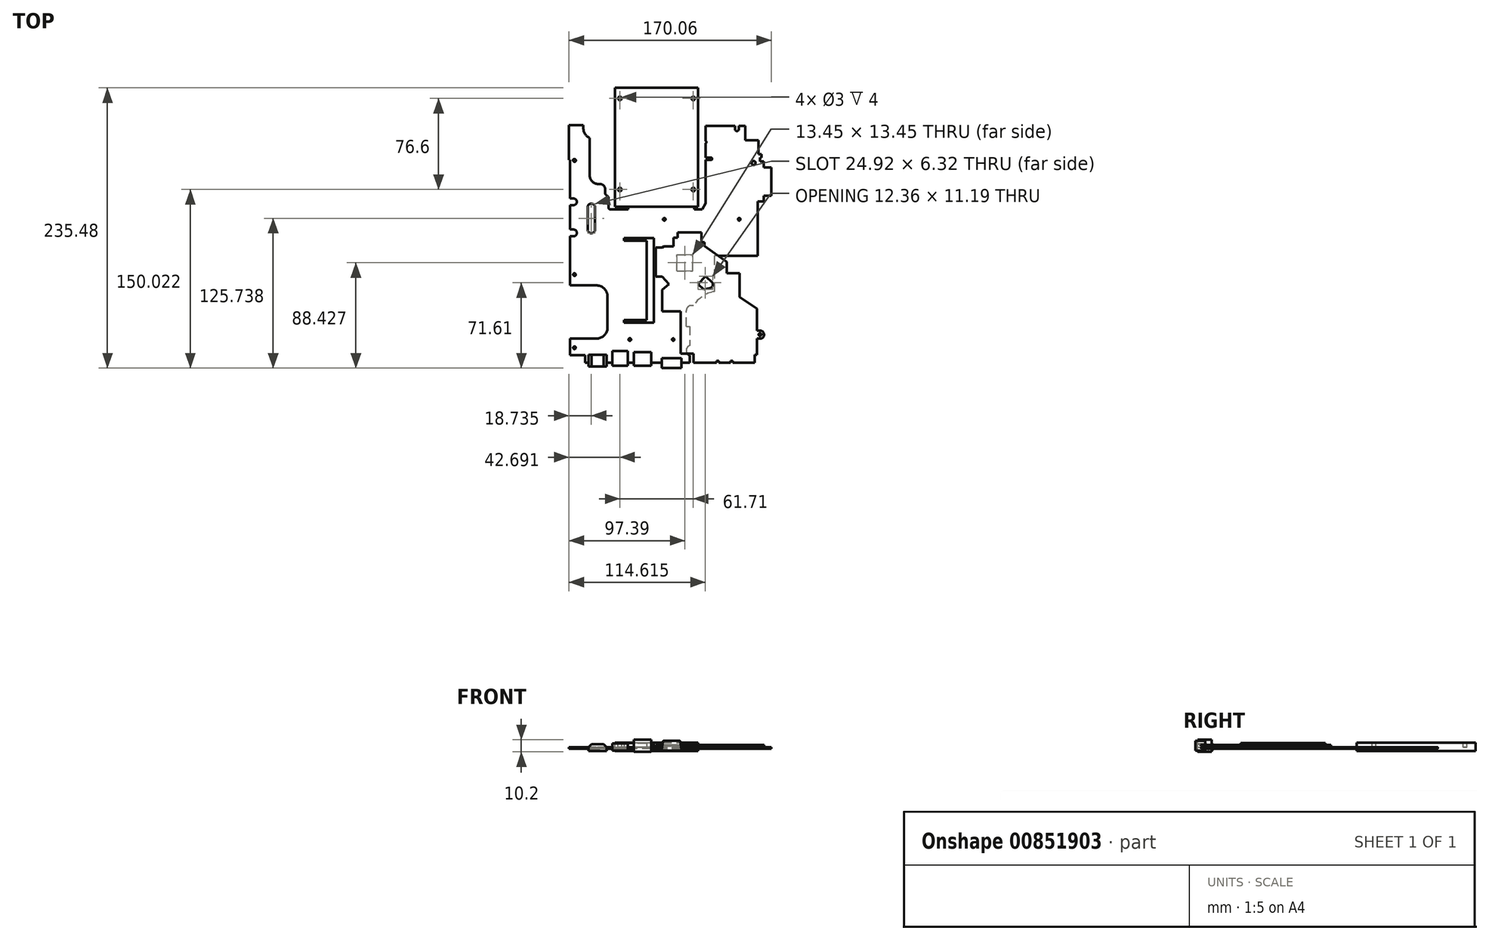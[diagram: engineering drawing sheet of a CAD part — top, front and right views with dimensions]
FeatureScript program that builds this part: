
annotation { "Feature Type Name" : "Feature", "Feature Type Description" : "" }
export const myFeature = defineFeature(function(context is Context, id is Id, definition is map)
    precondition{}
    {
        {
            var Q0;
            Q0=qCreatedBy(makeId("Top.planeOp"),FACE);
            var sketch = newSketch(context, id + "F0", { "sketchPlane" : qUnion([Q0])});
            skLineSegment(sketch, "E0.MirrorCS", {"start": v(161.8, 176.97) * mm, "end": v(160.62, 176.97) * mm});
            skLineSegment(sketch, "E1.MirrorCS", {"start": v(32.43, 144.35) * mm, "end": v(31.5, 145.13) * mm});
            skArc(sketch, "E2.MirrorCS", {"start": v(30.35, 147.11) * mm, "mid": v(30.65, 145.97) * mm, "end": v(31.5, 145.13) * mm});
            skLineSegment(sketch, "E3.MirrorCS", {"start": v(160.62, 176.97) * mm, "end": v(160.62, 173.55) * mm});
            skLineSegment(sketch, "E4.MirrorCS", {"start": v(160.62, 173.55) * mm, "end": v(163.56, 173.55) * mm});
            skArc(sketch, "E5.MirrorCS", {"start": v(32.43, 144.35) * mm, "mid": v(32.98, 143.62) * mm, "end": v(33.16, 142.73) * mm});
            skLineSegment(sketch, "E6.MirrorCS", {"start": v(161.8, 179.85) * mm, "end": v(161.8, 176.97) * mm});
            skArc(sketch, "E7.MirrorCS", {"start": v(139.53, 200.77) * mm, "mid": v(141.13, 199.17) * mm, "end": v(142.74, 200.77) * mm});
            skArc(sketch, "E8.MirrorCS", {"start": v(119.35, 174.82) * mm, "mid": v(120.35, 175.82) * mm, "end": v(119.35, 176.81) * mm});
            skLineSegment(sketch, "E9.MirrorCS", {"start": v(114.8, 174.82) * mm, "end": v(119.35, 174.82) * mm});
            skLineSegment(sketch, "E10.MirrorCS", {"start": v(163.56, 173.55) * mm, "end": v(163.56, 168.46) * mm});
            skLineSegment(sketch, "E11.MirrorCS", {"start": v(119.35, 176.81) * mm, "end": v(114.8, 176.81) * mm});
            skLineSegment(sketch, "E12.MirrorCS", {"start": v(159.15, 179.85) * mm, "end": v(161.8, 179.85) * mm});
            skArc(sketch, "E13.MirrorCS", {"start": v(114.8, 190.88) * mm, "mid": v(115.54, 189.87) * mm, "end": v(114.8, 188.87) * mm});
            skLineSegment(sketch, "E14.MirrorCS", {"start": v(0.74, 175.03) * mm, "end": v(0, 175.03) * mm});
            skLineSegment(sketch, "E15.MirrorCS", {"start": v(142.74, 200.77) * mm, "end": v(142.74, 203.6) * mm});
            skLineSegment(sketch, "E16.MirrorCS", {"start": v(139.53, 203.6) * mm, "end": v(139.53, 200.77) * mm});
            skLineSegment(sketch, "E17.MirrorCS", {"start": v(105.22, 135.48) * mm, "end": v(105.22, 133.25) * mm});
            skArc(sketch, "E18.MirrorCS", {"start": v(25.8, 154.73) * mm, "mid": v(28.8, 153.62) * mm, "end": v(30.35, 150.82) * mm});
            skLineSegment(sketch, "E19.MirrorCS", {"start": v(30.35, 150.82) * mm, "end": v(30.35, 147.11) * mm});
            skLineSegment(sketch, "E20.MirrorCS", {"start": v(3.74, 116.4) * mm, "end": v(0.74, 116.4) * mm});
            skArc(sketch, "E21.MirrorCS", {"start": v(12.01, 201.5) * mm, "mid": v(13.48, 196.59) * mm, "end": v(17.4, 193.28) * mm});
            skLineSegment(sketch, "E22.MirrorCS", {"start": v(49.62, 133.34) * mm, "end": v(49.62, 135.48) * mm});
            skArc(sketch, "E23.MirrorCS", {"start": v(102.62, 52.48) * mm, "mid": v(99.74, 51.25) * mm, "end": v(98.65, 48.32) * mm});
            skLineSegment(sketch, "E24.MirrorCS", {"start": v(148.18, 191.34) * mm, "end": v(159.15, 191.34) * mm});
            skArc(sketch, "E25.MirrorCS", {"start": v(21.9, 116.44) * mm, "mid": v(18.73, 113.28) * mm, "end": v(15.58, 116.44) * mm});
            skLineSegment(sketch, "E26.MirrorCS", {"start": v(105.22, 133.25) * mm, "end": v(112, 133.25) * mm});
            skArc(sketch, "E27.MirrorCS", {"start": v(17.4, 161.62) * mm, "mid": v(19.17, 157) * mm, "end": v(23.57, 154.73) * mm});
            skLineSegment(sketch, "E28.MirrorCS", {"start": v(101.34, 10.63) * mm, "end": v(101.34, 4.6) * mm});
            skLineSegment(sketch, "E29.MirrorCS", {"start": v(163.56, 144.81) * mm, "end": v(163.56, 139.94) * mm});
            skArc(sketch, "E30.MirrorCS", {"start": v(15.58, 135.04) * mm, "mid": v(18.73, 138.2) * mm, "end": v(21.9, 135.04) * mm});
            skLineSegment(sketch, "E31.MirrorCS", {"start": v(142.74, 203.6) * mm, "end": v(148.18, 203.6) * mm});
            skLineSegment(sketch, "E32.MirrorCS", {"start": v(0.74, 110.71) * mm, "end": v(3.74, 110.71) * mm});
            skLineSegment(sketch, "E33.MirrorCS", {"start": v(104.55, 52.48) * mm, "end": v(102.62, 52.48) * mm});
            skLineSegment(sketch, "E34.MirrorCS", {"start": v(98.65, 35.03) * mm, "end": v(101.34, 35.03) * mm});
            skLineSegment(sketch, "E35.MirrorCS", {"start": v(170.06, 144.81) * mm, "end": v(163.56, 144.81) * mm});
            skLineSegment(sketch, "E36.MirrorCS", {"start": v(12.01, 204.12) * mm, "end": v(12.01, 201.5) * mm});
            skCircle(sketch, "E37.MirrorC", {"center": v(4.56, 174.52) * mm, "radius": 1.2 * mm});
            skArc(sketch, "E38.MirrorCS", {"start": v(33.16, 134.9) * mm, "mid": v(33.7, 133.72) * mm, "end": v(34.94, 133.34) * mm});
            skLineSegment(sketch, "E39.MirrorCS", {"start": v(112, 133.25) * mm, "end": v(114.8, 138.53) * mm});
            skLineSegment(sketch, "E40.MirrorCS", {"start": v(23.57, 154.73) * mm, "end": v(25.8, 154.73) * mm});
            skArc(sketch, "E41.MirrorCS", {"start": v(101.34, 10.63) * mm, "mid": v(98.56, 14.75) * mm, "end": v(101.34, 18.86) * mm});
            skLineSegment(sketch, "E42.MirrorCS", {"start": v(163.56, 139.94) * mm, "end": v(158.48, 139.94) * mm});
            skLineSegment(sketch, "E43.MirrorCS", {"start": v(163.56, 168.46) * mm, "end": v(170.06, 168.46) * mm});
            skArc(sketch, "E44.MirrorCS", {"start": v(3.74, 110.71) * mm, "mid": v(6.59, 113.55) * mm, "end": v(3.74, 116.4) * mm});
            skArc(sketch, "E45.MirrorCS", {"start": v(3.74, 136.9) * mm, "mid": v(6.55, 139.7) * mm, "end": v(3.74, 142.51) * mm});
            skLineSegment(sketch, "E46.MirrorCS", {"start": v(159.15, 191.34) * mm, "end": v(159.15, 179.85) * mm});
            skLineSegment(sketch, "E47.MirrorCS", {"start": v(13.38, 10.75) * mm, "end": v(13.38, 4.6) * mm});
            skLineSegment(sketch, "E48.MirrorCS", {"start": v(3.74, 142.51) * mm, "end": v(0.74, 142.51) * mm});
            skLineSegment(sketch, "E49.MirrorCS", {"start": v(33.16, 142.73) * mm, "end": v(33.16, 134.9) * mm});
            skLineSegment(sketch, "E50.MirrorCS", {"start": v(0.74, 136.9) * mm, "end": v(3.74, 136.9) * mm});
            skCircle(sketch, "E51.MirrorC", {"center": v(143.06, 125.02) * mm, "radius": 1.1 * mm});
            skLineSegment(sketch, "E52.MirrorCS", {"start": v(0.74, 10.75) * mm, "end": v(0.74, 24.7) * mm});
            skLineSegment(sketch, "E53.MirrorCS", {"start": v(49.46, 14.2) * mm, "end": v(36.26, 14.2) * mm});
            skCircle(sketch, "E54.MirrorC", {"center": v(4.56, 17.02) * mm, "radius": 1.1 * mm});
            skCircle(sketch, "E55.MirrorC", {"center": v(155.16, 172.32) * mm, "radius": 1.7 * mm});
            skLineSegment(sketch, "E56.MirrorCS", {"start": v(0.74, 24.7) * mm, "end": v(22.83, 24.7) * mm});
            skCircle(sketch, "E57.MirrorC", {"center": v(51.06, 23.92) * mm, "radius": 1.1 * mm});
            skCircle(sketch, "E58.MirrorC", {"center": v(160.56, 28.02) * mm, "radius": 1.2 * mm});
            skLineSegment(sketch, "E59.MirrorCS", {"start": v(68.91, 13.4) * mm, "end": v(54.61, 13.4) * mm});
            skCircle(sketch, "E60.MirrorC", {"center": v(4.56, 78.52) * mm, "radius": 1.1 * mm});
            skCircle(sketch, "E61.MirrorC", {"center": v(87.56, 23.92) * mm, "radius": 1 * mm});
            skCircle(sketch, "E62.MirrorC", {"center": v(80.06, 125.02) * mm, "radius": 1.1 * mm});
            skLineSegment(sketch, "E63.MirrorCS", {"start": v(31.46, 11.1) * mm, "end": v(16.46, 11.1) * mm});
            skLineSegment(sketch, "E64.MirrorCS", {"start": v(13.38, 4.6) * mm, "end": v(101.34, 4.6) * mm});
            skLineSegment(sketch, "E65.MirrorCS", {"start": v(0, 175.03) * mm, "end": v(0, 204.12) * mm});
            skLineSegment(sketch, "E66.MirrorCS", {"start": v(21.9, 116.44) * mm, "end": v(21.9, 135.04) * mm});
            skLineSegment(sketch, "E67.MirrorCS", {"start": v(114.8, 176.81) * mm, "end": v(114.8, 188.87) * mm});
            skLineSegment(sketch, "E68.MirrorCS", {"start": v(0.74, 10.75) * mm, "end": v(13.38, 10.75) * mm});
            skArc(sketch, "E69.MirrorCS", {"start": v(32.29, 60.25) * mm, "mid": v(29.5, 66.84) * mm, "end": v(22.83, 69.42) * mm});
            skLineSegment(sketch, "E70.MirrorCS", {"start": v(49.62, 135.48) * mm, "end": v(105.22, 135.48) * mm});
            skLineSegment(sketch, "E71.MirrorCS", {"start": v(32.29, 32.81) * mm, "end": v(32.29, 60.25) * mm});
            skLineSegment(sketch, "E72.MirrorCS", {"start": v(0, 204.12) * mm, "end": v(12.01, 204.12) * mm});
            skLineSegment(sketch, "E73.MirrorCS", {"start": v(114.8, 190.88) * mm, "end": v(114.8, 203.6) * mm});
            skLineSegment(sketch, "E74.MirrorCS", {"start": v(22.83, 69.42) * mm, "end": v(0.74, 69.42) * mm});
            skLineSegment(sketch, "E75.MirrorCS", {"start": v(34.94, 133.34) * mm, "end": v(49.62, 133.34) * mm});
            skLineSegment(sketch, "E76.MirrorCS", {"start": v(158.48, 139.94) * mm, "end": v(158.48, 94.24) * mm});
            skArc(sketch, "E77.MirrorCS", {"start": v(22.83, 24.7) * mm, "mid": v(29.06, 27) * mm, "end": v(32.29, 32.81) * mm});
            skLineSegment(sketch, "E78.MirrorCS", {"start": v(148.18, 203.6) * mm, "end": v(148.18, 191.34) * mm});
            skLineSegment(sketch, "E79.MirrorCS", {"start": v(114.8, 203.6) * mm, "end": v(139.53, 203.6) * mm});
            skLineSegment(sketch, "E80.MirrorCS", {"start": v(114.8, 138.53) * mm, "end": v(114.8, 174.82) * mm});
            skLineSegment(sketch, "E81.MirrorCS", {"start": v(15.58, 116.44) * mm, "end": v(15.58, 135.04) * mm});
            skLineSegment(sketch, "E82.MirrorCS", {"start": v(122.04, 94.24) * mm, "end": v(122.04, 64.27) * mm});
            skLineSegment(sketch, "E83.MirrorCS", {"start": v(0.74, 116.4) * mm, "end": v(0.74, 136.9) * mm});
            skLineSegment(sketch, "E84.MirrorCS", {"start": v(0.74, 142.51) * mm, "end": v(0.74, 175.03) * mm});
            skLineSegment(sketch, "E85.MirrorCS", {"start": v(94.46, 8.2) * mm, "end": v(78.06, 8.2) * mm});
            skLineSegment(sketch, "E86.MirrorCS", {"start": v(98.65, 35.03) * mm, "end": v(98.65, 48.32) * mm});
            skArc(sketch, "E87.MirrorCS", {"start": v(104.55, 52.48) * mm, "mid": v(112.1, 60.16) * mm, "end": v(122.04, 64.27) * mm});
            skLineSegment(sketch, "E88.MirrorCS", {"start": v(158.48, 94.24) * mm, "end": v(122.04, 94.24) * mm});
            skLineSegment(sketch, "E89.MirrorCS", {"start": v(170.06, 168.46) * mm, "end": v(170.06, 144.81) * mm});
            skLineSegment(sketch, "E90.MirrorCS", {"start": v(0.74, 69.42) * mm, "end": v(0.74, 110.71) * mm});
            skLineSegment(sketch, "E91.MirrorCS", {"start": v(17.4, 193.28) * mm, "end": v(17.4, 161.62) * mm});
            skLineSegment(sketch, "E92.MirrorCS", {"start": v(101.34, 35.03) * mm, "end": v(101.34, 18.86) * mm});
            skPoint(sketch, "E93", {"position": v(23.96, 11.1) * mm});
            skPoint(sketch, "E94", {"position": v(42.86, 14.2) * mm});
            skPoint(sketch, "E95", {"position": v(61.76, 13.4) * mm});
            skPoint(sketch, "E96", {"position": v(86.26, 8.2) * mm});
            skLineSegment(sketch, "E97", {"start": v(94.46, 4.6) * mm, "end": v(94.46, 8.2) * mm});
            skLineSegment(sketch, "E98", {"start": v(78.06, 8.2) * mm, "end": v(78.06, 4.6) * mm});
            skLineSegment(sketch, "E99", {"start": v(68.91, 4.6) * mm, "end": v(68.91, 13.4) * mm});
            skLineSegment(sketch, "E100", {"start": v(54.61, 13.4) * mm, "end": v(54.61, 4.6) * mm});
            skLineSegment(sketch, "E101", {"start": v(49.46, 4.6) * mm, "end": v(49.46, 14.2) * mm});
            skLineSegment(sketch, "E102", {"start": v(36.26, 14.2) * mm, "end": v(36.26, 4.6) * mm});
            skLineSegment(sketch, "E103", {"start": v(31.46, 4.6) * mm, "end": v(31.46, 11.1) * mm});
            skLineSegment(sketch, "E104", {"start": v(16.46, 11.1) * mm, "end": v(16.46, 4.6) * mm});
            skPoint(sketch, "E105", {"position": v(77.42, 135.48) * mm});
            skSolve(sketch);
        }
        {
            var Q0;
            Q0=makeQuery(id+"F0.imprint","IMPRINT",FACE,{"disambiguationData":[TD([[makeQuery(id+"F0.imprint","IMPRINT",EDGE,{"derivedFrom":sQuery(id+"F0.wireOp",EDGE,"E0.MirrorCS")}),-1.0]])]});
            extrude(context, id + "F1", {"entities" : qUnion([Q0]), "depth" : 1 * mm, "offsetDistance" : 25 * mm});
        }
        {
            var Q0;
            Q0=makeQuery(id+"F1.opExtrude","CAP_FACE",FACE,{"disambiguationData":[OSD([sQuery(id+"F0.wireOp",EDGE,"E0.MirrorCS"),sQuery(id+"F0.wireOp",EDGE,"E1.MirrorCS"),sQuery(id+"F0.wireOp",EDGE,"E2.MirrorCS"),sQuery(id+"F0.wireOp",EDGE,"E3.MirrorCS"),sQuery(id+"F0.wireOp",EDGE,"E4.MirrorCS"),sQuery(id+"F0.wireOp",EDGE,"E5.MirrorCS"),sQuery(id+"F0.wireOp",EDGE,"E6.MirrorCS"),sQuery(id+"F0.wireOp",EDGE,"E7.MirrorCS"),sQuery(id+"F0.wireOp",EDGE,"E8.MirrorCS"),sQuery(id+"F0.wireOp",EDGE,"E9.MirrorCS"),sQuery(id+"F0.wireOp",EDGE,"E10.MirrorCS"),sQuery(id+"F0.wireOp",EDGE,"E11.MirrorCS"),sQuery(id+"F0.wireOp",EDGE,"E12.MirrorCS"),sQuery(id+"F0.wireOp",EDGE,"E13.MirrorCS"),sQuery(id+"F0.wireOp",EDGE,"E14.MirrorCS"),sQuery(id+"F0.wireOp",EDGE,"E15.MirrorCS"),sQuery(id+"F0.wireOp",EDGE,"E16.MirrorCS"),sQuery(id+"F0.wireOp",EDGE,"E17.MirrorCS"),sQuery(id+"F0.wireOp",EDGE,"E18.MirrorCS"),sQuery(id+"F0.wireOp",EDGE,"E19.MirrorCS"),sQuery(id+"F0.wireOp",EDGE,"E20.MirrorCS"),sQuery(id+"F0.wireOp",EDGE,"E21.MirrorCS"),sQuery(id+"F0.wireOp",EDGE,"E22.MirrorCS"),sQuery(id+"F0.wireOp",EDGE,"E23.MirrorCS"),sQuery(id+"F0.wireOp",EDGE,"E24.MirrorCS"),sQuery(id+"F0.wireOp",EDGE,"E25.MirrorCS"),sQuery(id+"F0.wireOp",EDGE,"E26.MirrorCS"),sQuery(id+"F0.wireOp",EDGE,"E27.MirrorCS"),sQuery(id+"F0.wireOp",EDGE,"E28.MirrorCS"),sQuery(id+"F0.wireOp",EDGE,"E29.MirrorCS"),sQuery(id+"F0.wireOp",EDGE,"E30.MirrorCS"),sQuery(id+"F0.wireOp",EDGE,"E31.MirrorCS"),sQuery(id+"F0.wireOp",EDGE,"E31.MirrorCS"),sQuery(id+"F0.wireOp",EDGE,"E32.MirrorCS"),sQuery(id+"F0.wireOp",EDGE,"E33.MirrorCS"),sQuery(id+"F0.wireOp",EDGE,"E34.MirrorCS"),sQuery(id+"F0.wireOp",EDGE,"E35.MirrorCS"),sQuery(id+"F0.wireOp",EDGE,"E36.MirrorCS"),sQuery(id+"F0.wireOp",EDGE,"E37.MirrorC"),sQuery(id+"F0.wireOp",EDGE,"E38.MirrorCS"),sQuery(id+"F0.wireOp",EDGE,"E39.MirrorCS"),sQuery(id+"F0.wireOp",EDGE,"E40.MirrorCS"),sQuery(id+"F0.wireOp",EDGE,"E41.MirrorCS"),sQuery(id+"F0.wireOp",EDGE,"E42.MirrorCS"),sQuery(id+"F0.wireOp",EDGE,"E43.MirrorCS"),sQuery(id+"F0.wireOp",EDGE,"E45.MirrorCS"),sQuery(id+"F0.wireOp",EDGE,"E44.MirrorCS"),sQuery(id+"F0.wireOp",EDGE,"E45.MirrorCS"),sQuery(id+"F0.wireOp",EDGE,"E46.MirrorCS"),sQuery(id+"F0.wireOp",EDGE,"E49.MirrorCS"),sQuery(id+"F0.wireOp",EDGE,"E47.MirrorCS"),sQuery(id+"F0.wireOp",EDGE,"E48.MirrorCS"),sQuery(id+"F0.wireOp",EDGE,"E49.MirrorCS"),sQuery(id+"F0.wireOp",EDGE,"E50.MirrorCS"),sQuery(id+"F0.wireOp",EDGE,"E54.MirrorCS"),sQuery(id+"F0.wireOp",EDGE,"E51.MirrorC"),sQuery(id+"F0.wireOp",EDGE,"E52.MirrorCS"),sQuery(id+"F0.wireOp",EDGE,"E53.MirrorCS"),sQuery(id+"F0.wireOp",EDGE,"E54.MirrorC"),sQuery(id+"F0.wireOp",EDGE,"E55.MirrorC"),sQuery(id+"F0.wireOp",EDGE,"E56.MirrorCS"),sQuery(id+"F0.wireOp",EDGE,"E61.MirrorCS"),sQuery(id+"F0.wireOp",EDGE,"E62.MirrorCS"),sQuery(id+"F0.wireOp",EDGE,"E57.MirrorC"),sQuery(id+"F0.wireOp",EDGE,"E59.MirrorCS"),sQuery(id+"F0.wireOp",EDGE,"E66.MirrorCS"),sQuery(id+"F0.wireOp",EDGE,"E60.MirrorC"),sQuery(id+"F0.wireOp",EDGE,"E61.MirrorC"),sQuery(id+"F0.wireOp",EDGE,"E62.MirrorC"),sQuery(id+"F0.wireOp",EDGE,"E63.MirrorCS"),sQuery(id+"F0.wireOp",EDGE,"E64.MirrorCS"),sQuery(id+"F0.wireOp",EDGE,"E72.MirrorCS"),sQuery(id+"F0.wireOp",EDGE,"E65.MirrorCS"),sQuery(id+"F0.wireOp",EDGE,"E66.MirrorCS"),sQuery(id+"F0.wireOp",EDGE,"E67.MirrorCS"),sQuery(id+"F0.wireOp",EDGE,"E68.MirrorCS"),sQuery(id+"F0.wireOp",EDGE,"E69.MirrorCS"),sQuery(id+"F0.wireOp",EDGE,"E70.MirrorCS"),sQuery(id+"F0.wireOp",EDGE,"E71.MirrorCS"),sQuery(id+"F0.wireOp",EDGE,"E72.MirrorCS"),sQuery(id+"F0.wireOp",EDGE,"E73.MirrorCS"),sQuery(id+"F0.wireOp",EDGE,"E74.MirrorCS"),sQuery(id+"F0.wireOp",EDGE,"E75.MirrorCS"),sQuery(id+"F0.wireOp",EDGE,"E76.MirrorCS"),sQuery(id+"F0.wireOp",EDGE,"E77.MirrorCS"),sQuery(id+"F0.wireOp",EDGE,"E78.MirrorCS"),sQuery(id+"F0.wireOp",EDGE,"E79.MirrorCS"),sQuery(id+"F0.wireOp",EDGE,"E80.MirrorCS"),sQuery(id+"F0.wireOp",EDGE,"E81.MirrorCS"),sQuery(id+"F0.wireOp",EDGE,"E82.MirrorCS"),sQuery(id+"F0.wireOp",EDGE,"E83.MirrorCS"),sQuery(id+"F0.wireOp",EDGE,"E84.MirrorCS"),sQuery(id+"F0.wireOp",EDGE,"E85.MirrorCS"),sQuery(id+"F0.wireOp",EDGE,"E86.MirrorCS"),sQuery(id+"F0.wireOp",EDGE,"E87.MirrorCS"),sQuery(id+"F0.wireOp",EDGE,"E88.MirrorCS"),sQuery(id+"F0.wireOp",EDGE,"E89.MirrorCS"),sQuery(id+"F0.wireOp",EDGE,"E90.MirrorCS"),sQuery(id+"F0.wireOp",EDGE,"E91.MirrorCS"),sQuery(id+"F0.wireOp",EDGE,"E92.MirrorCS")])],"isStart":false});
            var sketch = newSketch(context, id + "F2", { "sketchPlane" : qUnion([Q0])});
            skLineSegment(sketch, "E106.bottom", {"start": v(90.67, 81.7) * mm, "end": v(90.67, 95.15) * mm});
            skLineSegment(sketch, "E106.top", {"start": v(104.11, 81.7) * mm, "end": v(104.11, 95.15) * mm});
            skLineSegment(sketch, "E106.left", {"start": v(90.67, 81.7) * mm, "end": v(104.11, 81.7) * mm});
            skLineSegment(sketch, "E106.right", {"start": v(90.67, 95.15) * mm, "end": v(104.11, 95.15) * mm});
            skSolve(sketch);
        }
        {
            var Q0;
            Q0=makeQuery(id+"F2.imprint","IMPRINT",FACE,{"disambiguationData":[TD([[makeQuery(id+"F2.imprint","IMPRINT",EDGE,{"derivedFrom":sQuery(id+"F2.wireOp",EDGE,"E106.bottom")}),-1.0]])]});
            extrude(context, id + "F3", {"entities" : qUnion([Q0]), "operationType" : NewBodyOperationType.ADD, "depth" : 1 * mm, "offsetDistance" : 25 * mm});
        }
        {
            var Q0;
            Q0=makeQuery(id+"F3.opExtrude","CAP_FACE",FACE,{"disambiguationData":[OSD([sQuery(id+"F2.wireOp",EDGE,"E106.bottom"),sQuery(id+"F2.wireOp",EDGE,"E106.top"),sQuery(id+"F2.wireOp",EDGE,"E106.left"),sQuery(id+"F2.wireOp",EDGE,"E106.right")])],"isStart":false});
            var sketch = newSketch(context, id + "F4", { "sketchPlane" : qUnion([Q0])});
            skLineSegment(sketch, "E107", {"start": v(104.63, 4.3) * mm, "end": v(124.07, 4.3) * mm});
            skLineSegment(sketch, "E108", {"start": v(124.07, 4.3) * mm, "end": v(124.07, 6.13) * mm});
            skLineSegment(sketch, "E109", {"start": v(124.07, 6.13) * mm, "end": v(125.92, 6.13) * mm});
            skLineSegment(sketch, "E110", {"start": v(125.92, 6.13) * mm, "end": v(125.92, 4.3) * mm});
            skLineSegment(sketch, "E111", {"start": v(125.92, 4.3) * mm, "end": v(135.9, 4.3) * mm});
            skLineSegment(sketch, "E112", {"start": v(135.9, 4.3) * mm, "end": v(135.9, 6.13) * mm});
            skLineSegment(sketch, "E113", {"start": v(135.9, 6.13) * mm, "end": v(137.76, 6.13) * mm});
            skLineSegment(sketch, "E114", {"start": v(137.76, 6.13) * mm, "end": v(137.76, 4.3) * mm});
            skLineSegment(sketch, "E115", {"start": v(137.76, 4.3) * mm, "end": v(155.91, 4.3) * mm});
            skLineSegment(sketch, "E116", {"start": v(155.91, 4.3) * mm, "end": v(155.91, 11.15) * mm});
            skLineSegment(sketch, "E117", {"start": v(155.91, 11.15) * mm, "end": v(157.83, 11.15) * mm});
            skLineSegment(sketch, "E118", {"start": v(157.83, 11.15) * mm, "end": v(157.83, 24.62) * mm});
            skLineSegment(sketch, "E119", {"start": v(157.83, 24.62) * mm, "end": v(160.56, 24.62) * mm});
            skLineSegment(sketch, "E120", {"start": v(160.56, 31.42) * mm, "end": v(157.83, 31.42) * mm});
            skLineSegment(sketch, "E121", {"start": v(157.83, 31.42) * mm, "end": v(157.83, 49.9) * mm});
            skLineSegment(sketch, "E122", {"start": v(157.83, 49.9) * mm, "end": v(143.25, 59.63) * mm});
            skLineSegment(sketch, "E123", {"start": v(143.25, 59.63) * mm, "end": v(143.25, 79.71) * mm});
            skLineSegment(sketch, "E124", {"start": v(143.25, 79.71) * mm, "end": v(132.63, 79.71) * mm});
            skLineSegment(sketch, "E125", {"start": v(132.63, 79.71) * mm, "end": v(132.63, 89.3) * mm});
            skLineSegment(sketch, "E126", {"start": v(132.63, 89.3) * mm, "end": v(113.7, 102.48) * mm});
            skLineSegment(sketch, "E127", {"start": v(113.7, 102.48) * mm, "end": v(113.7, 105.68) * mm});
            skLineSegment(sketch, "E128", {"start": v(113.7, 105.68) * mm, "end": v(111.16, 105.68) * mm});
            skLineSegment(sketch, "E129", {"start": v(111.16, 105.68) * mm, "end": v(111.16, 113.93) * mm});
            skLineSegment(sketch, "E130", {"start": v(111.16, 113.93) * mm, "end": v(91.41, 113.93) * mm});
            skLineSegment(sketch, "E131", {"start": v(91.41, 113.93) * mm, "end": v(91.41, 109.62) * mm});
            skLineSegment(sketch, "E132", {"start": v(91.41, 109.62) * mm, "end": v(87.76, 109.62) * mm});
            skLineSegment(sketch, "E133", {"start": v(87.76, 109.62) * mm, "end": v(87.76, 102.3) * mm});
            skLineSegment(sketch, "E134", {"start": v(87.76, 102.3) * mm, "end": v(80.01, 102.3) * mm});
            skLineSegment(sketch, "E135", {"start": v(80.01, 102.3) * mm, "end": v(78.29, 101.34) * mm});
            skLineSegment(sketch, "E136", {"start": v(78.29, 101.34) * mm, "end": v(72.8, 101.34) * mm});
            skLineSegment(sketch, "E137", {"start": v(72.8, 101.34) * mm, "end": v(72.8, 76.7) * mm});
            skLineSegment(sketch, "E138", {"start": v(72.8, 76.7) * mm, "end": v(78.4, 76.7) * mm});
            skLineSegment(sketch, "E139", {"start": v(78.4, 76.7) * mm, "end": v(83.88, 70.57) * mm});
            skLineSegment(sketch, "E140", {"start": v(83.88, 70.57) * mm, "end": v(78.4, 65.66) * mm});
            skLineSegment(sketch, "E141", {"start": v(78.4, 65.66) * mm, "end": v(78.4, 47.77) * mm});
            skLineSegment(sketch, "E142", {"start": v(78.4, 47.77) * mm, "end": v(93.89, 47.77) * mm});
            skLineSegment(sketch, "E143", {"start": v(93.89, 47.77) * mm, "end": v(93.89, 12.06) * mm});
            skLineSegment(sketch, "E144", {"start": v(93.89, 12.06) * mm, "end": v(104.63, 12.06) * mm});
            skLineSegment(sketch, "E145", {"start": v(104.63, 12.06) * mm, "end": v(104.63, 4.3) * mm});
            skLineSegment(sketch, "E146", {"start": v(108.44, 70.6) * mm, "end": v(114.65, 77.2) * mm});
            skLineSegment(sketch, "E147", {"start": v(114.65, 77.2) * mm, "end": v(120.8, 71.42) * mm});
            skLineSegment(sketch, "E148", {"start": v(108.44, 70.6) * mm, "end": v(113.3, 66.02) * mm});
            skLineSegment(sketch, "E149", {"start": v(113.3, 66.02) * mm, "end": v(118.8, 67.32) * mm});
            skLineSegment(sketch, "E150", {"start": v(120.8, 69.85) * mm, "end": v(120.8, 71.42) * mm});
            skPoint(sketch, "E151.visualSharp", {"position": v(120.8, 67.8) * mm});
            skArc(sketch, "E151.filletArc", {"start": v(118.8, 67.32) * mm, "mid": v(120.23, 68.24) * mm, "end": v(120.8, 69.85) * mm});
            skCircle(sketch, "E152", {"center": v(160.56, 28.02) * mm, "radius": 1.18 * mm});
            skArc(sketch, "E153", {"start": v(160.56, 31.42) * mm, "mid": v(163.96, 28.02) * mm, "end": v(160.56, 24.62) * mm});
            skSolve(sketch);
        }
        {
            var Q0;
            Q0=makeQuery(id+"F4.imprint","IMPRINT",FACE,{"disambiguationData":[TD([[makeQuery(id+"F4.imprint","IMPRINT",EDGE,{"derivedFrom":sQuery(id+"F4.wireOp",EDGE,"E107")}),1.0]])]});
            var Q1;
            Q1=makeQuery(id+"F4.imprint","IMPRINT",FACE,{"disambiguationData":[TD([[makeQuery(id+"F4.imprint","IMPRINT",EDGE,{"derivedFrom":makeQuery(id+"F3.opExtrude","CAP_EDGE",EDGE,{"disambiguationData":[OSD([sQuery(id+"F2.wireOp",EDGE,"E106.bottom")])],"isStart":false})}),-1.0]])]});
            extrude(context, id + "F5", {"entities" : qUnion([Q0, Q1]), "operationType" : NewBodyOperationType.ADD, "depth" : 1 * mm, "offsetDistance" : 25 * mm});
        }
        {
            var Q0;
            Q0=makeQuery(id+"F1.opExtrude","CAP_FACE",FACE,{"disambiguationData":[OSD([sQuery(id+"F0.wireOp",EDGE,"E0.MirrorCS"),sQuery(id+"F0.wireOp",EDGE,"E1.MirrorCS"),sQuery(id+"F0.wireOp",EDGE,"E2.MirrorCS"),sQuery(id+"F0.wireOp",EDGE,"E3.MirrorCS"),sQuery(id+"F0.wireOp",EDGE,"E4.MirrorCS"),sQuery(id+"F0.wireOp",EDGE,"E5.MirrorCS"),sQuery(id+"F0.wireOp",EDGE,"E6.MirrorCS"),sQuery(id+"F0.wireOp",EDGE,"E7.MirrorCS"),sQuery(id+"F0.wireOp",EDGE,"E8.MirrorCS"),sQuery(id+"F0.wireOp",EDGE,"E9.MirrorCS"),sQuery(id+"F0.wireOp",EDGE,"E10.MirrorCS"),sQuery(id+"F0.wireOp",EDGE,"E11.MirrorCS"),sQuery(id+"F0.wireOp",EDGE,"E12.MirrorCS"),sQuery(id+"F0.wireOp",EDGE,"E13.MirrorCS"),sQuery(id+"F0.wireOp",EDGE,"E14.MirrorCS"),sQuery(id+"F0.wireOp",EDGE,"E15.MirrorCS"),sQuery(id+"F0.wireOp",EDGE,"E16.MirrorCS"),sQuery(id+"F0.wireOp",EDGE,"E17.MirrorCS"),sQuery(id+"F0.wireOp",EDGE,"E18.MirrorCS"),sQuery(id+"F0.wireOp",EDGE,"E19.MirrorCS"),sQuery(id+"F0.wireOp",EDGE,"E20.MirrorCS"),sQuery(id+"F0.wireOp",EDGE,"E21.MirrorCS"),sQuery(id+"F0.wireOp",EDGE,"E22.MirrorCS"),sQuery(id+"F0.wireOp",EDGE,"E23.MirrorCS"),sQuery(id+"F0.wireOp",EDGE,"E24.MirrorCS"),sQuery(id+"F0.wireOp",EDGE,"E25.MirrorCS"),sQuery(id+"F0.wireOp",EDGE,"E26.MirrorCS"),sQuery(id+"F0.wireOp",EDGE,"E27.MirrorCS"),sQuery(id+"F0.wireOp",EDGE,"E28.MirrorCS"),sQuery(id+"F0.wireOp",EDGE,"E29.MirrorCS"),sQuery(id+"F0.wireOp",EDGE,"E30.MirrorCS"),sQuery(id+"F0.wireOp",EDGE,"E31.MirrorCS"),sQuery(id+"F0.wireOp",EDGE,"E31.MirrorCS"),sQuery(id+"F0.wireOp",EDGE,"E32.MirrorCS"),sQuery(id+"F0.wireOp",EDGE,"E33.MirrorCS"),sQuery(id+"F0.wireOp",EDGE,"E34.MirrorCS"),sQuery(id+"F0.wireOp",EDGE,"E35.MirrorCS"),sQuery(id+"F0.wireOp",EDGE,"E36.MirrorCS"),sQuery(id+"F0.wireOp",EDGE,"E37.MirrorC"),sQuery(id+"F0.wireOp",EDGE,"E38.MirrorCS"),sQuery(id+"F0.wireOp",EDGE,"E39.MirrorCS"),sQuery(id+"F0.wireOp",EDGE,"E40.MirrorCS"),sQuery(id+"F0.wireOp",EDGE,"E41.MirrorCS"),sQuery(id+"F0.wireOp",EDGE,"E42.MirrorCS"),sQuery(id+"F0.wireOp",EDGE,"E43.MirrorCS"),sQuery(id+"F0.wireOp",EDGE,"E45.MirrorCS"),sQuery(id+"F0.wireOp",EDGE,"E44.MirrorCS"),sQuery(id+"F0.wireOp",EDGE,"E45.MirrorCS"),sQuery(id+"F0.wireOp",EDGE,"E46.MirrorCS"),sQuery(id+"F0.wireOp",EDGE,"E49.MirrorCS"),sQuery(id+"F0.wireOp",EDGE,"E47.MirrorCS"),sQuery(id+"F0.wireOp",EDGE,"E48.MirrorCS"),sQuery(id+"F0.wireOp",EDGE,"E49.MirrorCS"),sQuery(id+"F0.wireOp",EDGE,"E50.MirrorCS"),sQuery(id+"F0.wireOp",EDGE,"E54.MirrorCS"),sQuery(id+"F0.wireOp",EDGE,"E51.MirrorC"),sQuery(id+"F0.wireOp",EDGE,"E52.MirrorCS"),sQuery(id+"F0.wireOp",EDGE,"E53.MirrorCS"),sQuery(id+"F0.wireOp",EDGE,"E54.MirrorC"),sQuery(id+"F0.wireOp",EDGE,"E55.MirrorC"),sQuery(id+"F0.wireOp",EDGE,"E56.MirrorCS"),sQuery(id+"F0.wireOp",EDGE,"E61.MirrorCS"),sQuery(id+"F0.wireOp",EDGE,"E62.MirrorCS"),sQuery(id+"F0.wireOp",EDGE,"E57.MirrorC"),sQuery(id+"F0.wireOp",EDGE,"E59.MirrorCS"),sQuery(id+"F0.wireOp",EDGE,"E66.MirrorCS"),sQuery(id+"F0.wireOp",EDGE,"E60.MirrorC"),sQuery(id+"F0.wireOp",EDGE,"E61.MirrorC"),sQuery(id+"F0.wireOp",EDGE,"E62.MirrorC"),sQuery(id+"F0.wireOp",EDGE,"E63.MirrorCS"),sQuery(id+"F0.wireOp",EDGE,"E64.MirrorCS"),sQuery(id+"F0.wireOp",EDGE,"E72.MirrorCS"),sQuery(id+"F0.wireOp",EDGE,"E65.MirrorCS"),sQuery(id+"F0.wireOp",EDGE,"E66.MirrorCS"),sQuery(id+"F0.wireOp",EDGE,"E67.MirrorCS"),sQuery(id+"F0.wireOp",EDGE,"E68.MirrorCS"),sQuery(id+"F0.wireOp",EDGE,"E69.MirrorCS"),sQuery(id+"F0.wireOp",EDGE,"E70.MirrorCS"),sQuery(id+"F0.wireOp",EDGE,"E71.MirrorCS"),sQuery(id+"F0.wireOp",EDGE,"E72.MirrorCS"),sQuery(id+"F0.wireOp",EDGE,"E73.MirrorCS"),sQuery(id+"F0.wireOp",EDGE,"E74.MirrorCS"),sQuery(id+"F0.wireOp",EDGE,"E75.MirrorCS"),sQuery(id+"F0.wireOp",EDGE,"E76.MirrorCS"),sQuery(id+"F0.wireOp",EDGE,"E77.MirrorCS"),sQuery(id+"F0.wireOp",EDGE,"E78.MirrorCS"),sQuery(id+"F0.wireOp",EDGE,"E79.MirrorCS"),sQuery(id+"F0.wireOp",EDGE,"E80.MirrorCS"),sQuery(id+"F0.wireOp",EDGE,"E81.MirrorCS"),sQuery(id+"F0.wireOp",EDGE,"E82.MirrorCS"),sQuery(id+"F0.wireOp",EDGE,"E83.MirrorCS"),sQuery(id+"F0.wireOp",EDGE,"E84.MirrorCS"),sQuery(id+"F0.wireOp",EDGE,"E85.MirrorCS"),sQuery(id+"F0.wireOp",EDGE,"E86.MirrorCS"),sQuery(id+"F0.wireOp",EDGE,"E87.MirrorCS"),sQuery(id+"F0.wireOp",EDGE,"E88.MirrorCS"),sQuery(id+"F0.wireOp",EDGE,"E89.MirrorCS"),sQuery(id+"F0.wireOp",EDGE,"E90.MirrorCS"),sQuery(id+"F0.wireOp",EDGE,"E91.MirrorCS"),sQuery(id+"F0.wireOp",EDGE,"E92.MirrorCS")])],"isStart":false});
            var sketch = newSketch(context, id + "F6", { "sketchPlane" : qUnion([Q0])});
            skLineSegment(sketch, "E154", {"start": v(65.27, 40.19) * mm, "end": v(65.27, 106.94) * mm});
            skLineSegment(sketch, "E155", {"start": v(65.27, 106.94) * mm, "end": v(46.16, 106.94) * mm});
            skLineSegment(sketch, "E156", {"start": v(46.16, 106.94) * mm, "end": v(46.16, 109.13) * mm});
            skLineSegment(sketch, "E157", {"start": v(46.16, 109.13) * mm, "end": v(71.22, 109.13) * mm});
            skLineSegment(sketch, "E158", {"start": v(71.22, 109.13) * mm, "end": v(71.22, 38) * mm});
            skLineSegment(sketch, "E159", {"start": v(71.22, 38) * mm, "end": v(46.16, 38) * mm});
            skLineSegment(sketch, "E160", {"start": v(46.16, 38) * mm, "end": v(46.16, 40.19) * mm});
            skLineSegment(sketch, "E161", {"start": v(46.16, 40.19) * mm, "end": v(65.27, 40.19) * mm});
            skSolve(sketch);
        }
        {
            var Q0;
            Q0=makeQuery(id+"F6.imprint","IMPRINT",FACE,{"disambiguationData":[TD([[makeQuery(id+"F6.imprint","IMPRINT",EDGE,{"derivedFrom":sQuery(id+"F6.wireOp",EDGE,"E154")}),-1.0]])]});
            extrude(context, id + "F7", {"entities" : qUnion([Q0]), "operationType" : NewBodyOperationType.ADD, "depth" : 3.5 * mm, "offsetDistance" : 25 * mm});
        }
        {
            var Q0;
            Q0=makeQuery(id+"F1.opExtrude","SWEPT_FACE",FACE,{"disambiguationData":[OSD([sQuery(id+"F0.wireOp",EDGE,"E85.MirrorCS")])]});
            var sketch = newSketch(context, id + "F8", { "sketchPlane" : qUnion([Q0])});
            skLineSegment(sketch, "E162", {"start": v(86.26, -1.6) * mm, "end": v(86.26, 6.4) * mm, "construction": true});
            skPoint(sketch, "E162.startSnap0", {"position": v(86.26, 0) * mm});
            skLineSegment(sketch, "E163", {"start": v(86.26, -1.6) * mm, "end": v(93.86, -1.6) * mm});
            skLineSegment(sketch, "E164", {"start": v(93.86, -1.6) * mm, "end": v(93.86, -1) * mm, "construction": true});
            skLineSegment(sketch, "E165", {"start": v(93.86, -1) * mm, "end": v(93.06, 5.8) * mm, "construction": true});
            skLineSegment(sketch, "E166", {"start": v(93.86, -1) * mm, "end": v(94.46, -0.93) * mm, "construction": true});
            skLineSegment(sketch, "E167", {"start": v(93.06, 5.8) * mm, "end": v(93.66, 5.87) * mm, "construction": true});
            skArc(sketch, "E168", {"start": v(93.86, -1.6) * mm, "mid": v(94.31, -1.4) * mm, "end": v(94.46, -0.93) * mm});
            skLineSegment(sketch, "E169", {"start": v(94.46, -0.93) * mm, "end": v(93.66, 5.87) * mm});
            skArc(sketch, "E170", {"start": v(93.66, 5.87) * mm, "mid": v(93.46, 6.25) * mm, "end": v(93.06, 6.4) * mm});
            skLineSegment(sketch, "E171", {"start": v(93.06, 6.4) * mm, "end": v(86.26, 6.4) * mm});
            skLineSegment(sketch, "E172.MirrorCS", {"start": v(79.46, 6.4) * mm, "end": v(86.26, 6.4) * mm});
            skArc(sketch, "E173.MirrorCS", {"start": v(78.87, 5.87) * mm, "mid": v(79.06, 6.25) * mm, "end": v(79.46, 6.4) * mm});
            skLineSegment(sketch, "E174.MirrorCS", {"start": v(78.07, -0.93) * mm, "end": v(78.87, 5.87) * mm});
            skArc(sketch, "E175.MirrorCS", {"start": v(78.66, -1.6) * mm, "mid": v(78.21, -1.4) * mm, "end": v(78.07, -0.93) * mm});
            skLineSegment(sketch, "E176.MirrorCS", {"start": v(86.26, -1.6) * mm, "end": v(78.66, -1.6) * mm});
            skSolve(sketch);
        }
        {
            var Q0;
            Q0=makeQuery(id+"F8.imprint","IMPRINT",FACE,{"disambiguationData":[TD([[makeQuery(id+"F8.imprint","IMPRINT",EDGE,{"derivedFrom":sQuery(id+"F8.wireOp",EDGE,"E163")}),1.0]])]});
            var Q1;
            {var subQ0=sQuery(id+"F8.wireOp",EDGE,"E169");var subQ1=sQuery(id+"F0.wireOp",EDGE,"E85.MirrorCS");var subQ2=makeQuery(id+"F1.opExtrude","CAP_EDGE",EDGE,{"disambiguationData":[OSD([subQ1])],"isStart":true});var subQ3=makeQuery(id+"F8.imprint","INTERSECT",VERTEX,{"derivedFrom":[subQ2,subQ0]});Q1=makeQuery(id+"F8.imprint","IMPRINT",FACE,{"disambiguationData":[TD([[makeQuery(id+"F8.imprint","IMPRINT",EDGE,{"disambiguationData":[TD([[subQ3,-1.0]])],"derivedFrom":subQ0}),1.0]])]});}
            var Q2;
            {var subQ0=sQuery(id+"F8.wireOp",EDGE,"E170");Q2=makeQuery(id+"F8.imprint","IMPRINT",FACE,{"disambiguationData":[TD([[makeQuery(id+"F8.imprint","IMPRINT",EDGE,{"derivedFrom":subQ0}),1.0]])]});}
            extrude(context, id + "F9", {"entities" : qUnion([Q0, Q1, Q2]), "operationType" : NewBodyOperationType.ADD, "depth" : 8.2 * mm, "offsetDistance" : 25 * mm});
        }
        {
            var Q0;
            Q0=makeQuery(id+"F1.opExtrude","SWEPT_FACE",FACE,{"disambiguationData":[OSD([sQuery(id+"F0.wireOp",EDGE,"E59.MirrorCS")])]});
            var sketch = newSketch(context, id + "F10", { "sketchPlane" : qUnion([Q0])});
            skLineSegment(sketch, "E177", {"start": v(61.76, -2.8) * mm, "end": v(61.76, 7.4) * mm, "construction": true});
            skPoint(sketch, "E177.startSnap0", {"position": v(61.76, 0) * mm});
            skLineSegment(sketch, "E178", {"start": v(61.76, -2.8) * mm, "end": v(68.91, -2.8) * mm});
            skLineSegment(sketch, "E179", {"start": v(68.91, -2.8) * mm, "end": v(68.91, 7.4) * mm});
            skLineSegment(sketch, "E180", {"start": v(68.91, 7.4) * mm, "end": v(61.76, 7.4) * mm});
            skLineSegment(sketch, "E181.MirrorCS", {"start": v(54.61, 7.4) * mm, "end": v(61.76, 7.4) * mm});
            skLineSegment(sketch, "E182.MirrorCS", {"start": v(54.61, -2.8) * mm, "end": v(54.61, 7.4) * mm});
            skLineSegment(sketch, "E183.MirrorCS", {"start": v(61.76, -2.8) * mm, "end": v(54.61, -2.8) * mm});
            skSolve(sketch);
        }
        {
            var Q0;
            {var subQ1=sQuery(id+"F10.wireOp",EDGE,"E180");Q0=makeQuery(id+"F10.imprint","IMPRINT",FACE,{"disambiguationData":[TD([[makeQuery(id+"F10.imprint","IMPRINT",EDGE,{"derivedFrom":subQ1}),1.0]])]});}
            var Q1;
            {var subQ1=sQuery(id+"F0.wireOp",EDGE,"E59.MirrorCS");var subQ2=makeQuery(id+"F1.opExtrude","CAP_EDGE",EDGE,{"disambiguationData":[OSD([subQ1])],"isStart":true});Q1=makeQuery(id+"F10.imprint","IMPRINT",FACE,{"disambiguationData":[TD([[makeQuery(id+"F10.imprint","IMPRINT",EDGE,{"derivedFrom":subQ2}),-1.0]])]});}
            var Q2;
            {var subQ4=sQuery(id+"F10.wireOp",EDGE,"E178");Q2=makeQuery(id+"F10.imprint","IMPRINT",FACE,{"disambiguationData":[TD([[makeQuery(id+"F10.imprint","IMPRINT",EDGE,{"derivedFrom":subQ4}),1.0]])]});}
            extrude(context, id + "F11", {"entities" : qUnion([Q0, Q1, Q2]), "operationType" : NewBodyOperationType.ADD, "depth" : 11.5 * mm, "offsetDistance" : 25 * mm});
        }
        {
            var Q0;
            Q0=makeQuery(id+"F1.opExtrude","SWEPT_FACE",FACE,{"disambiguationData":[OSD([sQuery(id+"F0.wireOp",EDGE,"E53.MirrorCS")])]});
            var sketch = newSketch(context, id + "F12", { "sketchPlane" : qUnion([Q0])});
            skLineSegment(sketch, "E184", {"start": v(42.86, -1.6) * mm, "end": v(42.86, 4.2) * mm, "construction": true});
            skPoint(sketch, "E184.startSnap0", {"position": v(42.86, 0) * mm});
            skLineSegment(sketch, "E185", {"start": v(42.86, -1.6) * mm, "end": v(49.46, -1.6) * mm});
            skLineSegment(sketch, "E186", {"start": v(49.46, -1.6) * mm, "end": v(49.46, 4.2) * mm});
            skLineSegment(sketch, "E187", {"start": v(49.46, 4.2) * mm, "end": v(42.86, 4.2) * mm});
            skLineSegment(sketch, "E188.MirrorCS", {"start": v(36.26, 4.2) * mm, "end": v(42.86, 4.2) * mm});
            skLineSegment(sketch, "E189.MirrorCS", {"start": v(36.26, -1.6) * mm, "end": v(36.26, 4.2) * mm});
            skLineSegment(sketch, "E190.MirrorCS", {"start": v(42.86, -1.6) * mm, "end": v(36.26, -1.6) * mm});
            skSolve(sketch);
        }
        {
            var Q0;
            {var subQ1=sQuery(id+"F12.wireOp",EDGE,"E187");Q0=makeQuery(id+"F12.imprint","IMPRINT",FACE,{"disambiguationData":[TD([[makeQuery(id+"F12.imprint","IMPRINT",EDGE,{"derivedFrom":subQ1}),1.0]])]});}
            var Q1;
            {var subQ1=sQuery(id+"F0.wireOp",EDGE,"E53.MirrorCS");var subQ2=makeQuery(id+"F1.opExtrude","CAP_EDGE",EDGE,{"disambiguationData":[OSD([subQ1])],"isStart":true});Q1=makeQuery(id+"F12.imprint","IMPRINT",FACE,{"disambiguationData":[TD([[makeQuery(id+"F12.imprint","IMPRINT",EDGE,{"derivedFrom":subQ2}),-1.0]])]});}
            var Q2;
            {var subQ4=sQuery(id+"F12.wireOp",EDGE,"E185");Q2=makeQuery(id+"F12.imprint","IMPRINT",FACE,{"disambiguationData":[TD([[makeQuery(id+"F12.imprint","IMPRINT",EDGE,{"derivedFrom":subQ4}),1.0]])]});}
            extrude(context, id + "F13", {"entities" : qUnion([Q0, Q1, Q2]), "operationType" : NewBodyOperationType.ADD, "depth" : 12.25 * mm, "offsetDistance" : 25 * mm});
        }
        {
            var Q0;
            Q0=makeQuery(id+"F1.opExtrude","SWEPT_FACE",FACE,{"disambiguationData":[OSD([sQuery(id+"F0.wireOp",EDGE,"E63.MirrorCS")])]});
            var sketch = newSketch(context, id + "F14", { "sketchPlane" : qUnion([Q0])});
            skLineSegment(sketch, "E191", {"start": v(23.96, -2.1) * mm, "end": v(23.96, 3.55) * mm, "construction": true});
            skPoint(sketch, "E191.startSnap0", {"position": v(23.96, 0) * mm});
            skLineSegment(sketch, "E192", {"start": v(23.96, -2.1) * mm, "end": v(31.46, -2.1) * mm});
            skLineSegment(sketch, "E193", {"start": v(31.46, -2.1) * mm, "end": v(31.46, 1.05) * mm});
            skLineSegment(sketch, "E194", {"start": v(31.46, 1.05) * mm, "end": v(28.96, 3.55) * mm});
            skLineSegment(sketch, "E195", {"start": v(28.96, 3.55) * mm, "end": v(23.96, 3.55) * mm});
            skLineSegment(sketch, "E196.MirrorCS", {"start": v(18.96, 3.55) * mm, "end": v(23.96, 3.55) * mm});
            skLineSegment(sketch, "E197.MirrorCS", {"start": v(16.46, 1.05) * mm, "end": v(18.96, 3.55) * mm});
            skLineSegment(sketch, "E198.MirrorCS", {"start": v(16.46, -2.1) * mm, "end": v(16.46, 1.05) * mm});
            skLineSegment(sketch, "E199.MirrorCS", {"start": v(23.96, -2.1) * mm, "end": v(16.46, -2.1) * mm});
            skSolve(sketch);
        }
        {
            var Q0;
            {var subQ0=sQuery(id+"F14.wireOp",EDGE,"E194");Q0=makeQuery(id+"F14.imprint","IMPRINT",FACE,{"disambiguationData":[TD([[makeQuery(id+"F14.imprint","IMPRINT",EDGE,{"derivedFrom":subQ0}),1.0]])]});}
            var Q1;
            {var subQ1=sQuery(id+"F0.wireOp",EDGE,"E63.MirrorCS");var subQ2=makeQuery(id+"F1.opExtrude","CAP_EDGE",EDGE,{"disambiguationData":[OSD([subQ1])],"isStart":true});Q1=makeQuery(id+"F14.imprint","IMPRINT",FACE,{"disambiguationData":[TD([[makeQuery(id+"F14.imprint","IMPRINT",EDGE,{"derivedFrom":subQ2}),-1.0]])]});}
            var Q2;
            {var subQ3=sQuery(id+"F14.wireOp",EDGE,"E192");Q2=makeQuery(id+"F14.imprint","IMPRINT",FACE,{"disambiguationData":[TD([[makeQuery(id+"F14.imprint","IMPRINT",EDGE,{"derivedFrom":subQ3}),1.0]])]});}
            extrude(context, id + "F15", {"entities" : qUnion([Q0, Q1, Q2]), "operationType" : NewBodyOperationType.ADD, "depth" : 9.9 * mm, "offsetDistance" : 25 * mm});
        }
        {
            var Q0;
            Q0=makeQuery(id+"F1.opExtrude","SWEPT_FACE",FACE,{"disambiguationData":[OSD([sQuery(id+"F0.wireOp",EDGE,"E70.MirrorCS")])]});
            var sketch = newSketch(context, id + "F16", { "sketchPlane" : qUnion([Q0])});
            skLineSegment(sketch, "E200", {"start": v(-73.54, -2) * mm, "end": v(-73.54, 5) * mm, "construction": true});
            skLineSegment(sketch, "E201", {"start": v(-73.54, -2) * mm, "end": v(-38.62, -2) * mm});
            skLineSegment(sketch, "E202", {"start": v(-38.62, -2) * mm, "end": v(-38.62, 5) * mm});
            skLineSegment(sketch, "E203", {"start": v(-38.62, 5) * mm, "end": v(-73.54, 5) * mm});
            skLineSegment(sketch, "E204.MirrorCS", {"start": v(-108.47, 5) * mm, "end": v(-73.54, 5) * mm});
            skLineSegment(sketch, "E205.MirrorCS", {"start": v(-108.47, -2) * mm, "end": v(-108.47, 5) * mm});
            skLineSegment(sketch, "E206.MirrorCS", {"start": v(-73.54, -2) * mm, "end": v(-108.47, -2) * mm});
            skPoint(sketch, "E207", {"position": v(-77.42, 0) * mm});
            skSolve(sketch);
        }
        {
            var Q0;
            Q0=makeQuery(id+"F16.imprint","IMPRINT",FACE,{"disambiguationData":[TD([[makeQuery(id+"F16.imprint","IMPRINT",EDGE,{"derivedFrom":sQuery(id+"F16.wireOp",EDGE,"E201")}),1.0]])]});
            var Q1;
            {var subQ0=sQuery(id+"F0.wireOp",EDGE,"E70.MirrorCS");Q1=makeQuery(id+"F16.imprint","IMPRINT",FACE,{"disambiguationData":[TD([[makeQuery(id+"F16.imprint","IMPRINT",EDGE,{"derivedFrom":makeQuery(id+"F1.opExtrude","CAP_EDGE",EDGE,{"disambiguationData":[OSD([subQ0])],"isStart":true})}),-1.0]])]});}
            extrude(context, id + "F17", {"entities" : qUnion([Q0, Q1]), "operationType" : NewBodyOperationType.ADD, "depth" : 100 * mm, "offsetDistance" : 25 * mm});
        }
        {
            var Q0;
            Q0=makeQuery(id+"F17.opExtrude","SWEPT_FACE",FACE,{"disambiguationData":[OSD([sQuery(id+"F16.wireOp",EDGE,"E203"),sQuery(id+"F16.wireOp",EDGE,"E204.MirrorCS")])]});
            var sketch = newSketch(context, id + "F18", { "sketchPlane" : qUnion([Q0])});
            skCircle(sketch, "E208", {"center": v(104.4, 226.62) * mm, "radius": 1.5 * mm});
            skCircle(sketch, "E209", {"center": v(42.7, 226.62) * mm, "radius": 1.5 * mm});
            skCircle(sketch, "E210", {"center": v(104.4, 150.02) * mm, "radius": 1.5 * mm});
            skCircle(sketch, "E211", {"center": v(42.7, 150.02) * mm, "radius": 1.5 * mm});
            skPoint(sketch, "E212", {"position": v(73.54, 135.48) * mm});
            skSolve(sketch);
        }
        {
            var Q0;
            Q0=makeQuery(id+"F18.imprint","IMPRINT",FACE,{"disambiguationData":[TD([[makeQuery(id+"F18.imprint","IMPRINT",EDGE,{"derivedFrom":sQuery(id+"F18.wireOp",EDGE,"E210")}),1.0]])]});
            var Q1;
            Q1=makeQuery(id+"F18.imprint","IMPRINT",FACE,{"disambiguationData":[TD([[makeQuery(id+"F18.imprint","IMPRINT",EDGE,{"derivedFrom":sQuery(id+"F18.wireOp",EDGE,"E211")}),1.0]])]});
            var Q2;
            Q2=makeQuery(id+"F18.imprint","IMPRINT",FACE,{"disambiguationData":[TD([[makeQuery(id+"F18.imprint","IMPRINT",EDGE,{"derivedFrom":sQuery(id+"F18.wireOp",EDGE,"E209")}),1.0]])]});
            var Q3;
            Q3=makeQuery(id+"F18.imprint","IMPRINT",FACE,{"disambiguationData":[TD([[makeQuery(id+"F18.imprint","IMPRINT",EDGE,{"derivedFrom":sQuery(id+"F18.wireOp",EDGE,"E208")}),1.0]])]});
            extrude(context, id + "F19", {"entities" : qUnion([Q0, Q1, Q2, Q3]), "operationType" : NewBodyOperationType.REMOVE, "oppositeDirection" : true, "depth" : 4 * mm, "offsetDistance" : 25 * mm});
        }
    });
